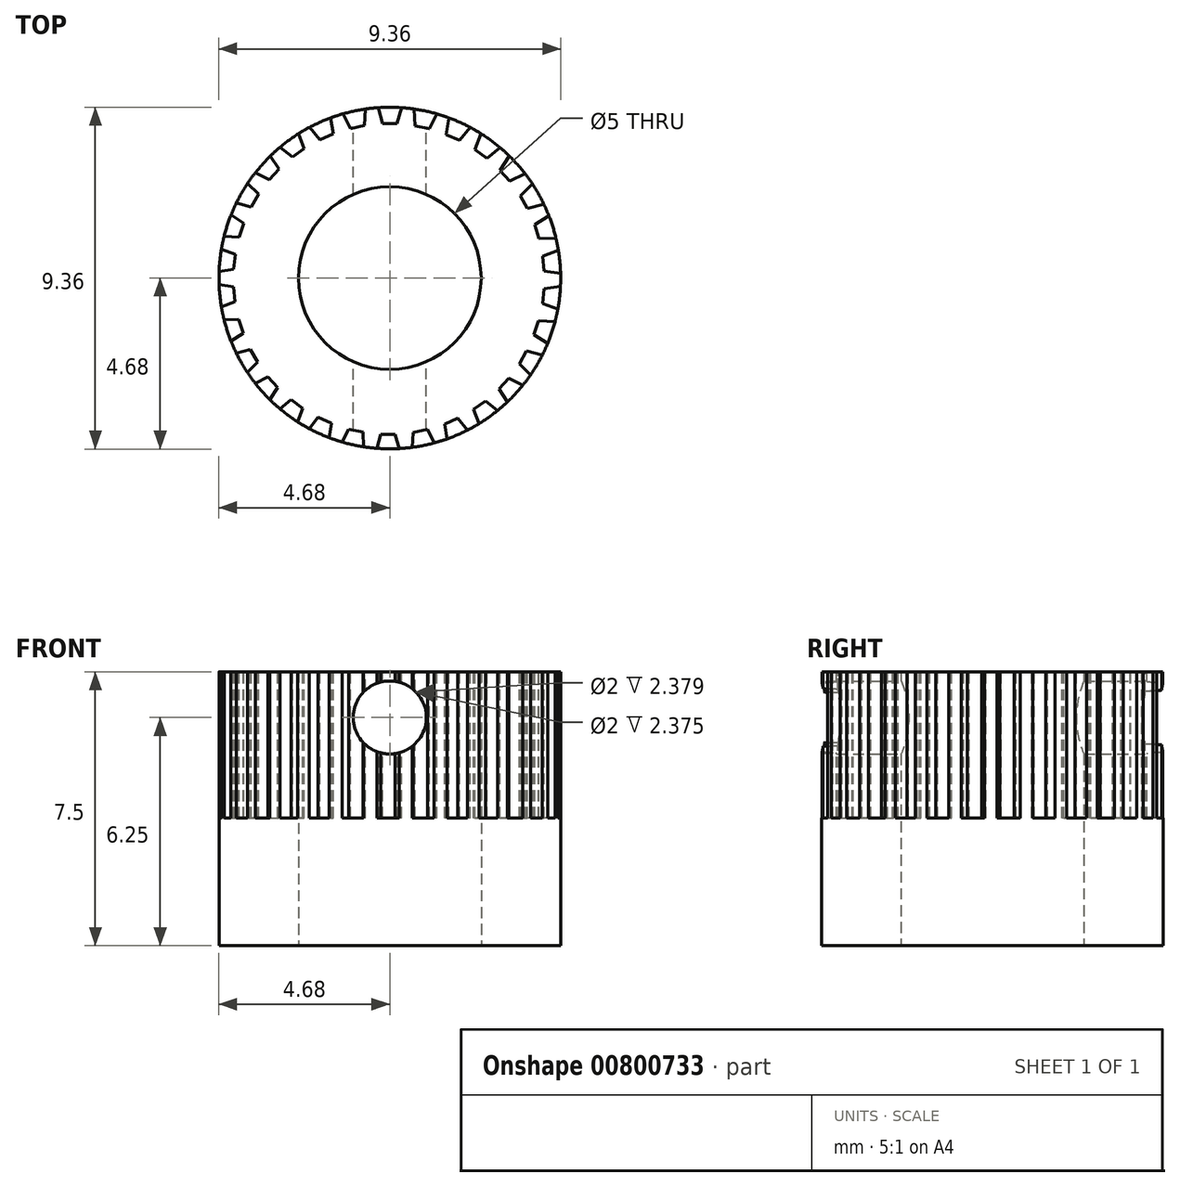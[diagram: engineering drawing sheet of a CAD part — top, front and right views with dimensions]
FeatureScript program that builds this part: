
annotation { "Feature Type Name" : "Feature", "Feature Type Description" : "" }
export const myFeature = defineFeature(function(context is Context, id is Id, definition is map)
    precondition{}
    {
        {
            var Q0;
            Q0=qCreatedBy(makeId("Top.planeOp"),FACE);
            var sketch = newSketch(context, id + "F0", { "sketchPlane" : qUnion([Q0])});
            skCircle(sketch, "E0", {"center": v(0, 0) * mm, "radius": 4.67 * mm});
            skCircle(sketch, "E1", {"center": v(0, 0) * mm, "radius": 2.5 * mm});
            skSolve(sketch);
        }
        {
            var Q0;
            Q0 = qSketchRegion(id + "F0", true);
            extrude(context, id + "F1", {"entities" : qUnion([Q0]), "depth" : 7.5 * mm, "offsetDistance" : 25 * mm});
        }
        {
            var Q0;
            Q0=makeQuery(id+"F1.opExtrude","CAP_FACE",FACE,{"disambiguationData":[OSD([sQuery(id+"F0.wireOp",EDGE,"E0"),sQuery(id+"F0.wireOp",EDGE,"E1")])],"isStart":false});
            var sketch = newSketch(context, id + "F2", { "sketchPlane" : qUnion([Q0])});
            skLineSegment(sketch, "E2", {"start": v(0, 5.22) * mm, "end": v(-0.47, 5.22) * mm});
            skLineSegment(sketch, "E3", {"start": v(-0.47, 5.22) * mm, "end": v(-0.2, 4.22) * mm});
            skLineSegment(sketch, "E4", {"start": v(-0.2, 4.22) * mm, "end": v(0, 4.22) * mm});
            skLineSegment(sketch, "E5", {"start": v(0, 4.22) * mm, "end": v(0, 5.22) * mm});
            skLineSegment(sketch, "E6.MirrorCS", {"start": v(0.2, 4.22) * mm, "end": v(0, 4.22) * mm});
            skLineSegment(sketch, "E7.MirrorCS", {"start": v(0, 5.22) * mm, "end": v(0.47, 5.22) * mm});
            skLineSegment(sketch, "E8.MirrorCS", {"start": v(0.47, 5.22) * mm, "end": v(0.2, 4.22) * mm});
            skLineSegment(sketch, "E9.1.0", {"start": v(-1.55, 5.02) * mm, "end": v(-1.08, 4.1) * mm});
            skLineSegment(sketch, "E9.1.1", {"start": v(-0.63, 5.21) * mm, "end": v(-0.69, 4.18) * mm});
            skLineSegment(sketch, "E9.1.2", {"start": v(-1.1, 5.12) * mm, "end": v(-0.63, 5.21) * mm});
            skLineSegment(sketch, "E9.1.3", {"start": v(-1.1, 5.12) * mm, "end": v(-1.55, 5.02) * mm});
            skLineSegment(sketch, "E9.1.4", {"start": v(-1.08, 4.1) * mm, "end": v(-0.88, 4.14) * mm});
            skLineSegment(sketch, "E9.1.5", {"start": v(-0.69, 4.18) * mm, "end": v(-0.88, 4.14) * mm});
            skLineSegment(sketch, "E9.2.0", {"start": v(-2.57, 4.6) * mm, "end": v(-1.91, 3.79) * mm});
            skLineSegment(sketch, "E9.2.1", {"start": v(-1.71, 4.97) * mm, "end": v(-1.55, 3.95) * mm});
            skLineSegment(sketch, "E9.2.2", {"start": v(-2.14, 4.78) * mm, "end": v(-1.71, 4.97) * mm});
            skLineSegment(sketch, "E9.2.3", {"start": v(-2.14, 4.78) * mm, "end": v(-2.57, 4.6) * mm});
            skLineSegment(sketch, "E9.2.4", {"start": v(-1.91, 3.79) * mm, "end": v(-1.73, 3.87) * mm});
            skLineSegment(sketch, "E9.2.5", {"start": v(-1.55, 3.95) * mm, "end": v(-1.73, 3.87) * mm});
            skLineSegment(sketch, "E9.3.0", {"start": v(-3.47, 3.96) * mm, "end": v(-2.66, 3.31) * mm});
            skLineSegment(sketch, "E9.3.1", {"start": v(-2.71, 4.51) * mm, "end": v(-2.34, 3.55) * mm});
            skLineSegment(sketch, "E9.3.2", {"start": v(-3.1, 4.24) * mm, "end": v(-2.71, 4.51) * mm});
            skLineSegment(sketch, "E9.3.3", {"start": v(-3.1, 4.24) * mm, "end": v(-3.47, 3.96) * mm});
            skLineSegment(sketch, "E9.3.4", {"start": v(-2.66, 3.31) * mm, "end": v(-2.5, 3.43) * mm});
            skLineSegment(sketch, "E9.3.5", {"start": v(-2.34, 3.55) * mm, "end": v(-2.5, 3.43) * mm});
            skLineSegment(sketch, "E9.4.0", {"start": v(-4.22, 3.16) * mm, "end": v(-3.3, 2.69) * mm});
            skLineSegment(sketch, "E9.4.1", {"start": v(-3.6, 3.85) * mm, "end": v(-3.03, 2.99) * mm});
            skLineSegment(sketch, "E9.4.2", {"start": v(-3.9, 3.5) * mm, "end": v(-3.6, 3.85) * mm});
            skLineSegment(sketch, "E9.4.3", {"start": v(-3.9, 3.5) * mm, "end": v(-4.22, 3.16) * mm});
            skLineSegment(sketch, "E9.4.4", {"start": v(-3.3, 2.69) * mm, "end": v(-3.17, 2.84) * mm});
            skLineSegment(sketch, "E9.4.5", {"start": v(-3.03, 2.99) * mm, "end": v(-3.17, 2.84) * mm});
            skLineSegment(sketch, "E9.5.0", {"start": v(-4.8, 2.22) * mm, "end": v(-3.8, 1.95) * mm});
            skLineSegment(sketch, "E9.5.1", {"start": v(-4.33, 3.03) * mm, "end": v(-3.6, 2.3) * mm});
            skLineSegment(sketch, "E9.5.2", {"start": v(-4.56, 2.62) * mm, "end": v(-4.33, 3.03) * mm});
            skLineSegment(sketch, "E9.5.3", {"start": v(-4.56, 2.62) * mm, "end": v(-4.8, 2.22) * mm});
            skLineSegment(sketch, "E9.5.4", {"start": v(-3.8, 1.95) * mm, "end": v(-3.7, 2.12) * mm});
            skLineSegment(sketch, "E9.5.5", {"start": v(-3.6, 2.3) * mm, "end": v(-3.7, 2.12) * mm});
            skLineSegment(sketch, "E9.6.0", {"start": v(-5.15, 1.18) * mm, "end": v(-4.12, 1.12) * mm});
            skLineSegment(sketch, "E9.6.1", {"start": v(-4.87, 2.07) * mm, "end": v(-4, 1.5) * mm});
            skLineSegment(sketch, "E9.6.2", {"start": v(-5.01, 1.62) * mm, "end": v(-4.87, 2.07) * mm});
            skLineSegment(sketch, "E9.6.3", {"start": v(-5.01, 1.62) * mm, "end": v(-5.15, 1.18) * mm});
            skLineSegment(sketch, "E9.6.4", {"start": v(-4.12, 1.12) * mm, "end": v(-4.06, 1.31) * mm});
            skLineSegment(sketch, "E9.6.5", {"start": v(-4, 1.5) * mm, "end": v(-4.06, 1.31) * mm});
            skLineSegment(sketch, "E9.7.0", {"start": v(-5.3, 0.08) * mm, "end": v(-4.27, 0.25) * mm});
            skLineSegment(sketch, "E9.7.1", {"start": v(-5.2, 1.01) * mm, "end": v(-4.23, 0.64) * mm});
            skLineSegment(sketch, "E9.7.2", {"start": v(-5.24, 0.55) * mm, "end": v(-5.2, 1.01) * mm});
            skLineSegment(sketch, "E9.7.3", {"start": v(-5.24, 0.55) * mm, "end": v(-5.3, 0.08) * mm});
            skLineSegment(sketch, "E9.7.4", {"start": v(-4.27, 0.25) * mm, "end": v(-4.25, 0.44) * mm});
            skLineSegment(sketch, "E9.7.5", {"start": v(-4.23, 0.64) * mm, "end": v(-4.25, 0.44) * mm});
            skLineSegment(sketch, "E9.8.0", {"start": v(-5.2, -1.01) * mm, "end": v(-4.23, -0.64) * mm});
            skLineSegment(sketch, "E9.8.1", {"start": v(-5.3, -0.08) * mm, "end": v(-4.28, -0.25) * mm});
            skLineSegment(sketch, "E9.8.2", {"start": v(-5.25, -0.55) * mm, "end": v(-5.3, -0.08) * mm});
            skLineSegment(sketch, "E9.8.3", {"start": v(-5.25, -0.55) * mm, "end": v(-5.2, -1.01) * mm});
            skLineSegment(sketch, "E9.8.4", {"start": v(-4.23, -0.64) * mm, "end": v(-4.25, -0.44) * mm});
            skLineSegment(sketch, "E9.8.5", {"start": v(-4.28, -0.25) * mm, "end": v(-4.25, -0.44) * mm});
            skLineSegment(sketch, "E9.9.0", {"start": v(-4.88, -2.07) * mm, "end": v(-4.01, -1.5) * mm});
            skLineSegment(sketch, "E9.9.1", {"start": v(-5.17, -1.18) * mm, "end": v(-4.14, -1.12) * mm});
            skLineSegment(sketch, "E9.9.2", {"start": v(-5.03, -1.62) * mm, "end": v(-5.17, -1.18) * mm});
            skLineSegment(sketch, "E9.9.3", {"start": v(-5.03, -1.62) * mm, "end": v(-4.88, -2.07) * mm});
            skLineSegment(sketch, "E9.9.4", {"start": v(-4.01, -1.5) * mm, "end": v(-4.07, -1.31) * mm});
            skLineSegment(sketch, "E9.9.5", {"start": v(-4.14, -1.12) * mm, "end": v(-4.07, -1.31) * mm});
            skLineSegment(sketch, "E9.10.0", {"start": v(-4.35, -3.03) * mm, "end": v(-3.62, -2.3) * mm});
            skLineSegment(sketch, "E9.10.1", {"start": v(-4.82, -2.22) * mm, "end": v(-3.82, -1.96) * mm});
            skLineSegment(sketch, "E9.10.2", {"start": v(-4.58, -2.63) * mm, "end": v(-4.82, -2.22) * mm});
            skLineSegment(sketch, "E9.10.3", {"start": v(-4.58, -2.63) * mm, "end": v(-4.35, -3.03) * mm});
            skLineSegment(sketch, "E9.10.4", {"start": v(-3.62, -2.3) * mm, "end": v(-3.72, -2.13) * mm});
            skLineSegment(sketch, "E9.10.5", {"start": v(-3.82, -1.96) * mm, "end": v(-3.72, -2.13) * mm});
            skLineSegment(sketch, "E9.11.0", {"start": v(-3.63, -3.87) * mm, "end": v(-3.07, -3) * mm});
            skLineSegment(sketch, "E9.11.1", {"start": v(-4.26, -3.17) * mm, "end": v(-3.33, -2.7) * mm});
            skLineSegment(sketch, "E9.11.2", {"start": v(-3.94, -3.52) * mm, "end": v(-4.26, -3.17) * mm});
            skLineSegment(sketch, "E9.11.3", {"start": v(-3.94, -3.52) * mm, "end": v(-3.63, -3.87) * mm});
            skLineSegment(sketch, "E9.11.4", {"start": v(-3.07, -3) * mm, "end": v(-3.2, -2.85) * mm});
            skLineSegment(sketch, "E9.11.5", {"start": v(-3.33, -2.7) * mm, "end": v(-3.2, -2.85) * mm});
            skLineSegment(sketch, "E9.12.0", {"start": v(-2.75, -4.53) * mm, "end": v(-2.38, -3.57) * mm});
            skLineSegment(sketch, "E9.12.1", {"start": v(-3.5, -3.98) * mm, "end": v(-2.7, -3.33) * mm});
            skLineSegment(sketch, "E9.12.2", {"start": v(-3.13, -4.26) * mm, "end": v(-3.5, -3.98) * mm});
            skLineSegment(sketch, "E9.12.3", {"start": v(-3.13, -4.26) * mm, "end": v(-2.75, -4.53) * mm});
            skLineSegment(sketch, "E9.12.4", {"start": v(-2.38, -3.57) * mm, "end": v(-2.54, -3.45) * mm});
            skLineSegment(sketch, "E9.12.5", {"start": v(-2.7, -3.33) * mm, "end": v(-2.54, -3.45) * mm});
            skLineSegment(sketch, "E9.13.0", {"start": v(-1.76, -5) * mm, "end": v(-1.6, -3.98) * mm});
            skLineSegment(sketch, "E9.13.1", {"start": v(-2.61, -4.62) * mm, "end": v(-1.96, -3.82) * mm});
            skLineSegment(sketch, "E9.13.2", {"start": v(-2.18, -4.81) * mm, "end": v(-2.61, -4.62) * mm});
            skLineSegment(sketch, "E9.13.3", {"start": v(-2.18, -4.81) * mm, "end": v(-1.76, -5) * mm});
            skLineSegment(sketch, "E9.13.4", {"start": v(-1.6, -3.98) * mm, "end": v(-1.78, -3.9) * mm});
            skLineSegment(sketch, "E9.13.5", {"start": v(-1.96, -3.82) * mm, "end": v(-1.78, -3.9) * mm});
            skLineSegment(sketch, "E9.14.0", {"start": v(-0.68, -5.25) * mm, "end": v(-0.74, -4.22) * mm});
            skLineSegment(sketch, "E9.14.1", {"start": v(-1.6, -5.06) * mm, "end": v(-1.13, -4.14) * mm});
            skLineSegment(sketch, "E9.14.2", {"start": v(-1.14, -5.16) * mm, "end": v(-1.6, -5.06) * mm});
            skLineSegment(sketch, "E9.14.3", {"start": v(-1.14, -5.16) * mm, "end": v(-0.68, -5.25) * mm});
            skLineSegment(sketch, "E9.14.4", {"start": v(-0.74, -4.22) * mm, "end": v(-0.93, -4.18) * mm});
            skLineSegment(sketch, "E9.14.5", {"start": v(-1.13, -4.14) * mm, "end": v(-0.93, -4.18) * mm});
            skLineSegment(sketch, "E9.15.0", {"start": v(0.42, -5.27) * mm, "end": v(0.15, -4.27) * mm});
            skLineSegment(sketch, "E9.15.1", {"start": v(-0.52, -5.27) * mm, "end": v(-0.25, -4.27) * mm});
            skLineSegment(sketch, "E9.15.2", {"start": v(-0.05, -5.28) * mm, "end": v(-0.52, -5.28) * mm});
            skLineSegment(sketch, "E9.15.3", {"start": v(-0.05, -5.27) * mm, "end": v(0.42, -5.27) * mm});
            skLineSegment(sketch, "E9.15.4", {"start": v(0.15, -4.28) * mm, "end": v(-0.05, -4.28) * mm});
            skLineSegment(sketch, "E9.15.5", {"start": v(-0.25, -4.28) * mm, "end": v(-0.05, -4.28) * mm});
            skLineSegment(sketch, "E9.16.0", {"start": v(1.5, -5.07) * mm, "end": v(1.03, -4.15) * mm});
            skLineSegment(sketch, "E9.16.1", {"start": v(0.58, -5.26) * mm, "end": v(0.64, -4.23) * mm});
            skLineSegment(sketch, "E9.16.2", {"start": v(1.04, -5.17) * mm, "end": v(0.58, -5.26) * mm});
            skLineSegment(sketch, "E9.16.3", {"start": v(1.04, -5.17) * mm, "end": v(1.5, -5.07) * mm});
            skLineSegment(sketch, "E9.16.4", {"start": v(1.03, -4.15) * mm, "end": v(0.83, -4.19) * mm});
            skLineSegment(sketch, "E9.16.5", {"start": v(0.64, -4.23) * mm, "end": v(0.83, -4.19) * mm});
            skLineSegment(sketch, "E9.17.0", {"start": v(2.52, -4.64) * mm, "end": v(1.86, -3.84) * mm});
            skLineSegment(sketch, "E9.17.1", {"start": v(1.66, -5.02) * mm, "end": v(1.5, -4) * mm});
            skLineSegment(sketch, "E9.17.2", {"start": v(2.09, -4.83) * mm, "end": v(1.66, -5.02) * mm});
            skLineSegment(sketch, "E9.17.3", {"start": v(2.09, -4.83) * mm, "end": v(2.52, -4.64) * mm});
            skLineSegment(sketch, "E9.17.4", {"start": v(1.86, -3.84) * mm, "end": v(1.68, -3.92) * mm});
            skLineSegment(sketch, "E9.17.5", {"start": v(1.5, -4) * mm, "end": v(1.68, -3.92) * mm});
            skLineSegment(sketch, "E9.18.0", {"start": v(3.42, -4.01) * mm, "end": v(2.61, -3.36) * mm});
            skLineSegment(sketch, "E9.18.1", {"start": v(2.66, -4.56) * mm, "end": v(2.3, -3.6) * mm});
            skLineSegment(sketch, "E9.18.2", {"start": v(3.04, -4.29) * mm, "end": v(2.66, -4.56) * mm});
            skLineSegment(sketch, "E9.18.3", {"start": v(3.04, -4.29) * mm, "end": v(3.42, -4.01) * mm});
            skLineSegment(sketch, "E9.18.4", {"start": v(2.61, -3.36) * mm, "end": v(2.45, -3.48) * mm});
            skLineSegment(sketch, "E9.18.5", {"start": v(2.3, -3.6) * mm, "end": v(2.45, -3.48) * mm});
            skLineSegment(sketch, "E9.19.0", {"start": v(4.17, -3.2) * mm, "end": v(3.25, -2.74) * mm});
            skLineSegment(sketch, "E9.19.1", {"start": v(3.55, -3.9) * mm, "end": v(2.98, -3.04) * mm});
            skLineSegment(sketch, "E9.19.2", {"start": v(3.86, -3.56) * mm, "end": v(3.55, -3.9) * mm});
            skLineSegment(sketch, "E9.19.3", {"start": v(3.86, -3.56) * mm, "end": v(4.17, -3.2) * mm});
            skLineSegment(sketch, "E9.19.4", {"start": v(3.25, -2.74) * mm, "end": v(3.12, -2.89) * mm});
            skLineSegment(sketch, "E9.19.5", {"start": v(2.98, -3.04) * mm, "end": v(3.12, -2.89) * mm});
            skLineSegment(sketch, "E9.20.0", {"start": v(4.74, -2.27) * mm, "end": v(3.74, -2) * mm});
            skLineSegment(sketch, "E9.20.1", {"start": v(4.28, -3.08) * mm, "end": v(3.54, -2.34) * mm});
            skLineSegment(sketch, "E9.20.2", {"start": v(4.5, -2.67) * mm, "end": v(4.28, -3.08) * mm});
            skLineSegment(sketch, "E9.20.3", {"start": v(4.5, -2.67) * mm, "end": v(4.74, -2.27) * mm});
            skLineSegment(sketch, "E9.20.4", {"start": v(3.74, -2) * mm, "end": v(3.64, -2.17) * mm});
            skLineSegment(sketch, "E9.20.5", {"start": v(3.54, -2.34) * mm, "end": v(3.64, -2.17) * mm});
            skLineSegment(sketch, "E9.21.0", {"start": v(5.1, -1.23) * mm, "end": v(4.07, -1.17) * mm});
            skLineSegment(sketch, "E9.21.1", {"start": v(4.82, -2.12) * mm, "end": v(3.95, -1.55) * mm});
            skLineSegment(sketch, "E9.21.2", {"start": v(4.96, -1.67) * mm, "end": v(4.82, -2.12) * mm});
            skLineSegment(sketch, "E9.21.3", {"start": v(4.96, -1.67) * mm, "end": v(5.1, -1.23) * mm});
            skLineSegment(sketch, "E9.21.4", {"start": v(4.07, -1.17) * mm, "end": v(4, -1.36) * mm});
            skLineSegment(sketch, "E9.21.5", {"start": v(3.95, -1.55) * mm, "end": v(4, -1.36) * mm});
            skLineSegment(sketch, "E9.22.0", {"start": v(5.24, -0.13) * mm, "end": v(4.22, -0.3) * mm});
            skLineSegment(sketch, "E9.22.1", {"start": v(5.14, -1.06) * mm, "end": v(4.18, -0.7) * mm});
            skLineSegment(sketch, "E9.22.2", {"start": v(5.2, -0.6) * mm, "end": v(5.14, -1.06) * mm});
            skLineSegment(sketch, "E9.22.3", {"start": v(5.2, -0.6) * mm, "end": v(5.24, -0.13) * mm});
            skLineSegment(sketch, "E9.22.4", {"start": v(4.22, -0.3) * mm, "end": v(4.2, -0.5) * mm});
            skLineSegment(sketch, "E9.22.5", {"start": v(4.18, -0.7) * mm, "end": v(4.2, -0.5) * mm});
            skLineSegment(sketch, "E9.23.0", {"start": v(5.15, 0.96) * mm, "end": v(4.18, 0.6) * mm});
            skLineSegment(sketch, "E9.23.1", {"start": v(5.25, 0.03) * mm, "end": v(4.23, 0.2) * mm});
            skLineSegment(sketch, "E9.23.2", {"start": v(5.2, 0.5) * mm, "end": v(5.25, 0.03) * mm});
            skLineSegment(sketch, "E9.23.3", {"start": v(5.2, 0.5) * mm, "end": v(5.15, 0.96) * mm});
            skLineSegment(sketch, "E9.23.4", {"start": v(4.18, 0.6) * mm, "end": v(4.2, 0.4) * mm});
            skLineSegment(sketch, "E9.23.5", {"start": v(4.23, 0.2) * mm, "end": v(4.2, 0.4) * mm});
            skLineSegment(sketch, "E9.24.0", {"start": v(4.83, 2.02) * mm, "end": v(3.96, 1.45) * mm});
            skLineSegment(sketch, "E9.24.1", {"start": v(5.12, 1.13) * mm, "end": v(4.09, 1.07) * mm});
            skLineSegment(sketch, "E9.24.2", {"start": v(4.98, 1.57) * mm, "end": v(5.12, 1.13) * mm});
            skLineSegment(sketch, "E9.24.3", {"start": v(4.98, 1.57) * mm, "end": v(4.83, 2.02) * mm});
            skLineSegment(sketch, "E9.24.4", {"start": v(3.96, 1.45) * mm, "end": v(4.02, 1.26) * mm});
            skLineSegment(sketch, "E9.24.5", {"start": v(4.09, 1.07) * mm, "end": v(4.02, 1.26) * mm});
            skLineSegment(sketch, "E9.25.0", {"start": v(4.3, 2.98) * mm, "end": v(3.57, 2.25) * mm});
            skLineSegment(sketch, "E9.25.1", {"start": v(4.77, 2.17) * mm, "end": v(3.77, 1.9) * mm});
            skLineSegment(sketch, "E9.25.2", {"start": v(4.53, 2.58) * mm, "end": v(4.77, 2.17) * mm});
            skLineSegment(sketch, "E9.25.3", {"start": v(4.53, 2.58) * mm, "end": v(4.3, 2.98) * mm});
            skLineSegment(sketch, "E9.25.4", {"start": v(3.57, 2.25) * mm, "end": v(3.67, 2.08) * mm});
            skLineSegment(sketch, "E9.25.5", {"start": v(3.77, 1.9) * mm, "end": v(3.67, 2.08) * mm});
            skLineSegment(sketch, "E9.26.0", {"start": v(3.58, 3.82) * mm, "end": v(3.02, 2.95) * mm});
            skLineSegment(sketch, "E9.26.1", {"start": v(4.2, 3.12) * mm, "end": v(3.28, 2.65) * mm});
            skLineSegment(sketch, "E9.26.2", {"start": v(3.9, 3.47) * mm, "end": v(4.2, 3.12) * mm});
            skLineSegment(sketch, "E9.26.3", {"start": v(3.9, 3.47) * mm, "end": v(3.58, 3.82) * mm});
            skLineSegment(sketch, "E9.26.4", {"start": v(3.02, 2.95) * mm, "end": v(3.15, 2.8) * mm});
            skLineSegment(sketch, "E9.26.5", {"start": v(3.28, 2.65) * mm, "end": v(3.15, 2.8) * mm});
            skLineSegment(sketch, "E9.27.0", {"start": v(2.7, 4.48) * mm, "end": v(2.33, 3.52) * mm});
            skLineSegment(sketch, "E9.27.1", {"start": v(3.46, 3.93) * mm, "end": v(2.66, 3.28) * mm});
            skLineSegment(sketch, "E9.27.2", {"start": v(3.08, 4.2) * mm, "end": v(3.46, 3.93) * mm});
            skLineSegment(sketch, "E9.27.3", {"start": v(3.08, 4.2) * mm, "end": v(2.7, 4.48) * mm});
            skLineSegment(sketch, "E9.27.4", {"start": v(2.33, 3.52) * mm, "end": v(2.5, 3.4) * mm});
            skLineSegment(sketch, "E9.27.5", {"start": v(2.66, 3.28) * mm, "end": v(2.5, 3.4) * mm});
            skLineSegment(sketch, "E9.28.0", {"start": v(1.7, 4.95) * mm, "end": v(1.54, 3.93) * mm});
            skLineSegment(sketch, "E9.28.1", {"start": v(2.56, 4.57) * mm, "end": v(1.9, 3.77) * mm});
            skLineSegment(sketch, "E9.28.2", {"start": v(2.13, 4.76) * mm, "end": v(2.56, 4.57) * mm});
            skLineSegment(sketch, "E9.28.3", {"start": v(2.13, 4.76) * mm, "end": v(1.7, 4.95) * mm});
            skLineSegment(sketch, "E9.28.4", {"start": v(1.54, 3.93) * mm, "end": v(1.73, 3.85) * mm});
            skLineSegment(sketch, "E9.28.5", {"start": v(1.9, 3.77) * mm, "end": v(1.73, 3.85) * mm});
            skLineSegment(sketch, "E9.29.0", {"start": v(0.63, 5.2) * mm, "end": v(0.69, 4.17) * mm});
            skLineSegment(sketch, "E9.29.1", {"start": v(1.55, 5) * mm, "end": v(1.08, 4.09) * mm});
            skLineSegment(sketch, "E9.29.2", {"start": v(1.1, 5.1) * mm, "end": v(1.55, 5) * mm});
            skLineSegment(sketch, "E9.29.3", {"start": v(1.1, 5.1) * mm, "end": v(0.63, 5.2) * mm});
            skLineSegment(sketch, "E9.29.4", {"start": v(0.69, 4.17) * mm, "end": v(0.88, 4.13) * mm});
            skLineSegment(sketch, "E9.29.5", {"start": v(1.08, 4.09) * mm, "end": v(0.88, 4.13) * mm});
            skPoint(sketch, "E9.center", {"position": v(-0.02, -0.02) * mm});
            skSolve(sketch);
        }
        {
            var Q0;
            {var subQ1=sQuery(id+"F2.wireOp",EDGE,"E9.12.4");Q0=makeQuery(id+"F2.imprint","IMPRINT",FACE,{"disambiguationData":[TD([[makeQuery(id+"F2.imprint","IMPRINT",EDGE,{"derivedFrom":subQ1}),1.0]])]});}
            var Q1;
            {var subQ6=sQuery(id+"F2.wireOp",EDGE,"E9.13.4");Q1=makeQuery(id+"F2.imprint","IMPRINT",FACE,{"disambiguationData":[TD([[makeQuery(id+"F2.imprint","IMPRINT",EDGE,{"derivedFrom":subQ6}),1.0]])]});}
            var Q2;
            {var subQ1=sQuery(id+"F2.wireOp",EDGE,"E9.14.4");Q2=makeQuery(id+"F2.imprint","IMPRINT",FACE,{"disambiguationData":[TD([[makeQuery(id+"F2.imprint","IMPRINT",EDGE,{"derivedFrom":subQ1}),1.0]])]});}
            var Q3;
            {var subQ1=sQuery(id+"F2.wireOp",EDGE,"E9.15.4");Q3=makeQuery(id+"F2.imprint","IMPRINT",FACE,{"disambiguationData":[TD([[makeQuery(id+"F2.imprint","IMPRINT",EDGE,{"derivedFrom":subQ1}),1.0]])]});}
            var Q4;
            {var subQ1=sQuery(id+"F2.wireOp",EDGE,"E9.11.4");Q4=makeQuery(id+"F2.imprint","IMPRINT",FACE,{"disambiguationData":[TD([[makeQuery(id+"F2.imprint","IMPRINT",EDGE,{"derivedFrom":subQ1}),1.0]])]});}
            var Q5;
            {var subQ1=sQuery(id+"F2.wireOp",EDGE,"E9.10.4");Q5=makeQuery(id+"F2.imprint","IMPRINT",FACE,{"disambiguationData":[TD([[makeQuery(id+"F2.imprint","IMPRINT",EDGE,{"derivedFrom":subQ1}),1.0]])]});}
            var Q6;
            {var subQ1=sQuery(id+"F2.wireOp",EDGE,"E9.9.4");Q6=makeQuery(id+"F2.imprint","IMPRINT",FACE,{"disambiguationData":[TD([[makeQuery(id+"F2.imprint","IMPRINT",EDGE,{"derivedFrom":subQ1}),1.0]])]});}
            var Q7;
            {var subQ1=sQuery(id+"F2.wireOp",EDGE,"E9.8.4");Q7=makeQuery(id+"F2.imprint","IMPRINT",FACE,{"disambiguationData":[TD([[makeQuery(id+"F2.imprint","IMPRINT",EDGE,{"derivedFrom":subQ1}),1.0]])]});}
            var Q8;
            {var subQ1=sQuery(id+"F2.wireOp",EDGE,"E9.7.4");Q8=makeQuery(id+"F2.imprint","IMPRINT",FACE,{"disambiguationData":[TD([[makeQuery(id+"F2.imprint","IMPRINT",EDGE,{"derivedFrom":subQ1}),1.0]])]});}
            var Q9;
            {var subQ1=sQuery(id+"F2.wireOp",EDGE,"E9.6.4");Q9=makeQuery(id+"F2.imprint","IMPRINT",FACE,{"disambiguationData":[TD([[makeQuery(id+"F2.imprint","IMPRINT",EDGE,{"derivedFrom":subQ1}),1.0]])]});}
            var Q10;
            {var subQ1=sQuery(id+"F2.wireOp",EDGE,"E9.5.4");Q10=makeQuery(id+"F2.imprint","IMPRINT",FACE,{"disambiguationData":[TD([[makeQuery(id+"F2.imprint","IMPRINT",EDGE,{"derivedFrom":subQ1}),1.0]])]});}
            var Q11;
            {var subQ1=sQuery(id+"F2.wireOp",EDGE,"E9.4.4");Q11=makeQuery(id+"F2.imprint","IMPRINT",FACE,{"disambiguationData":[TD([[makeQuery(id+"F2.imprint","IMPRINT",EDGE,{"derivedFrom":subQ1}),1.0]])]});}
            var Q12;
            {var subQ1=sQuery(id+"F2.wireOp",EDGE,"E9.3.4");Q12=makeQuery(id+"F2.imprint","IMPRINT",FACE,{"disambiguationData":[TD([[makeQuery(id+"F2.imprint","IMPRINT",EDGE,{"derivedFrom":subQ1}),1.0]])]});}
            var Q13;
            {var subQ6=sQuery(id+"F2.wireOp",EDGE,"E9.2.4");Q13=makeQuery(id+"F2.imprint","IMPRINT",FACE,{"disambiguationData":[TD([[makeQuery(id+"F2.imprint","IMPRINT",EDGE,{"derivedFrom":subQ6}),1.0]])]});}
            var Q14;
            {var subQ1=sQuery(id+"F2.wireOp",EDGE,"E9.1.4");Q14=makeQuery(id+"F2.imprint","IMPRINT",FACE,{"disambiguationData":[TD([[makeQuery(id+"F2.imprint","IMPRINT",EDGE,{"derivedFrom":subQ1}),1.0]])]});}
            var Q15;
            {var subQ0=sQuery(id+"F2.wireOp",EDGE,"E4");Q15=makeQuery(id+"F2.imprint","IMPRINT",FACE,{"disambiguationData":[TD([[makeQuery(id+"F2.imprint","IMPRINT",EDGE,{"derivedFrom":subQ0}),1.0]])]});}
            var Q16;
            {var subQ0=sQuery(id+"F2.wireOp",EDGE,"E6.MirrorCS");Q16=makeQuery(id+"F2.imprint","IMPRINT",FACE,{"disambiguationData":[TD([[makeQuery(id+"F2.imprint","IMPRINT",EDGE,{"derivedFrom":subQ0}),-1.0]])]});}
            var Q17;
            {var subQ1=sQuery(id+"F2.wireOp",EDGE,"E9.51.4");Q17=makeQuery(id+"F2.imprint","IMPRINT",FACE,{"disambiguationData":[TD([[makeQuery(id+"F2.imprint","IMPRINT",EDGE,{"derivedFrom":subQ1}),1.0]])]});}
            var Q18;
            {var subQ1=sQuery(id+"F2.wireOp",EDGE,"E9.50.4");Q18=makeQuery(id+"F2.imprint","IMPRINT",FACE,{"disambiguationData":[TD([[makeQuery(id+"F2.imprint","IMPRINT",EDGE,{"derivedFrom":subQ1}),1.0]])]});}
            var Q19;
            {var subQ1=sQuery(id+"F2.wireOp",EDGE,"E9.49.4");Q19=makeQuery(id+"F2.imprint","IMPRINT",FACE,{"disambiguationData":[TD([[makeQuery(id+"F2.imprint","IMPRINT",EDGE,{"derivedFrom":subQ1}),1.0]])]});}
            var Q20;
            {var subQ1=sQuery(id+"F2.wireOp",EDGE,"E9.48.4");Q20=makeQuery(id+"F2.imprint","IMPRINT",FACE,{"disambiguationData":[TD([[makeQuery(id+"F2.imprint","IMPRINT",EDGE,{"derivedFrom":subQ1}),1.0]])]});}
            var Q21;
            {var subQ1=sQuery(id+"F2.wireOp",EDGE,"E9.47.4");Q21=makeQuery(id+"F2.imprint","IMPRINT",FACE,{"disambiguationData":[TD([[makeQuery(id+"F2.imprint","IMPRINT",EDGE,{"derivedFrom":subQ1}),1.0]])]});}
            var Q22;
            {var subQ6=sQuery(id+"F2.wireOp",EDGE,"E9.46.4");Q22=makeQuery(id+"F2.imprint","IMPRINT",FACE,{"disambiguationData":[TD([[makeQuery(id+"F2.imprint","IMPRINT",EDGE,{"derivedFrom":subQ6}),1.0]])]});}
            var Q23;
            {var subQ1=sQuery(id+"F2.wireOp",EDGE,"E9.45.4");Q23=makeQuery(id+"F2.imprint","IMPRINT",FACE,{"disambiguationData":[TD([[makeQuery(id+"F2.imprint","IMPRINT",EDGE,{"derivedFrom":subQ1}),1.0]])]});}
            var Q24;
            {var subQ1=sQuery(id+"F2.wireOp",EDGE,"E9.44.4");Q24=makeQuery(id+"F2.imprint","IMPRINT",FACE,{"disambiguationData":[TD([[makeQuery(id+"F2.imprint","IMPRINT",EDGE,{"derivedFrom":subQ1}),1.0]])]});}
            var Q25;
            {var subQ1=sQuery(id+"F2.wireOp",EDGE,"E9.43.4");Q25=makeQuery(id+"F2.imprint","IMPRINT",FACE,{"disambiguationData":[TD([[makeQuery(id+"F2.imprint","IMPRINT",EDGE,{"derivedFrom":subQ1}),1.0]])]});}
            var Q26;
            {var subQ1=sQuery(id+"F2.wireOp",EDGE,"E9.42.4");Q26=makeQuery(id+"F2.imprint","IMPRINT",FACE,{"disambiguationData":[TD([[makeQuery(id+"F2.imprint","IMPRINT",EDGE,{"derivedFrom":subQ1}),1.0]])]});}
            var Q27;
            {var subQ1=sQuery(id+"F2.wireOp",EDGE,"E9.41.4");Q27=makeQuery(id+"F2.imprint","IMPRINT",FACE,{"disambiguationData":[TD([[makeQuery(id+"F2.imprint","IMPRINT",EDGE,{"derivedFrom":subQ1}),1.0]])]});}
            var Q28;
            {var subQ1=sQuery(id+"F2.wireOp",EDGE,"E9.40.4");Q28=makeQuery(id+"F2.imprint","IMPRINT",FACE,{"disambiguationData":[TD([[makeQuery(id+"F2.imprint","IMPRINT",EDGE,{"derivedFrom":subQ1}),1.0]])]});}
            var Q29;
            {var subQ1=sQuery(id+"F2.wireOp",EDGE,"E9.39.4");Q29=makeQuery(id+"F2.imprint","IMPRINT",FACE,{"disambiguationData":[TD([[makeQuery(id+"F2.imprint","IMPRINT",EDGE,{"derivedFrom":subQ1}),1.0]])]});}
            var Q30;
            {var subQ1=sQuery(id+"F2.wireOp",EDGE,"E9.38.4");Q30=makeQuery(id+"F2.imprint","IMPRINT",FACE,{"disambiguationData":[TD([[makeQuery(id+"F2.imprint","IMPRINT",EDGE,{"derivedFrom":subQ1}),1.0]])]});}
            var Q31;
            {var subQ1=sQuery(id+"F2.wireOp",EDGE,"E9.37.4");Q31=makeQuery(id+"F2.imprint","IMPRINT",FACE,{"disambiguationData":[TD([[makeQuery(id+"F2.imprint","IMPRINT",EDGE,{"derivedFrom":subQ1}),1.0]])]});}
            var Q32;
            {var subQ1=sQuery(id+"F2.wireOp",EDGE,"E9.36.4");Q32=makeQuery(id+"F2.imprint","IMPRINT",FACE,{"disambiguationData":[TD([[makeQuery(id+"F2.imprint","IMPRINT",EDGE,{"derivedFrom":subQ1}),1.0]])]});}
            var Q33;
            {var subQ6=sQuery(id+"F2.wireOp",EDGE,"E9.35.4");Q33=makeQuery(id+"F2.imprint","IMPRINT",FACE,{"disambiguationData":[TD([[makeQuery(id+"F2.imprint","IMPRINT",EDGE,{"derivedFrom":subQ6}),1.0]])]});}
            var Q34;
            {var subQ1=sQuery(id+"F2.wireOp",EDGE,"E9.34.4");Q34=makeQuery(id+"F2.imprint","IMPRINT",FACE,{"disambiguationData":[TD([[makeQuery(id+"F2.imprint","IMPRINT",EDGE,{"derivedFrom":subQ1}),1.0]])]});}
            var Q35;
            {var subQ1=sQuery(id+"F2.wireOp",EDGE,"E9.33.4");Q35=makeQuery(id+"F2.imprint","IMPRINT",FACE,{"disambiguationData":[TD([[makeQuery(id+"F2.imprint","IMPRINT",EDGE,{"derivedFrom":subQ1}),1.0]])]});}
            var Q36;
            {var subQ1=sQuery(id+"F2.wireOp",EDGE,"E9.32.4");Q36=makeQuery(id+"F2.imprint","IMPRINT",FACE,{"disambiguationData":[TD([[makeQuery(id+"F2.imprint","IMPRINT",EDGE,{"derivedFrom":subQ1}),1.0]])]});}
            var Q37;
            {var subQ1=sQuery(id+"F2.wireOp",EDGE,"E9.31.4");Q37=makeQuery(id+"F2.imprint","IMPRINT",FACE,{"disambiguationData":[TD([[makeQuery(id+"F2.imprint","IMPRINT",EDGE,{"derivedFrom":subQ1}),1.0]])]});}
            var Q38;
            {var subQ1=sQuery(id+"F2.wireOp",EDGE,"E9.30.4");Q38=makeQuery(id+"F2.imprint","IMPRINT",FACE,{"disambiguationData":[TD([[makeQuery(id+"F2.imprint","IMPRINT",EDGE,{"derivedFrom":subQ1}),1.0]])]});}
            var Q39;
            {var subQ1=sQuery(id+"F2.wireOp",EDGE,"E9.29.4");Q39=makeQuery(id+"F2.imprint","IMPRINT",FACE,{"disambiguationData":[TD([[makeQuery(id+"F2.imprint","IMPRINT",EDGE,{"derivedFrom":subQ1}),1.0]])]});}
            var Q40;
            {var subQ1=sQuery(id+"F2.wireOp",EDGE,"E9.28.4");Q40=makeQuery(id+"F2.imprint","IMPRINT",FACE,{"disambiguationData":[TD([[makeQuery(id+"F2.imprint","IMPRINT",EDGE,{"derivedFrom":subQ1}),1.0]])]});}
            var Q41;
            {var subQ1=sQuery(id+"F2.wireOp",EDGE,"E9.27.4");Q41=makeQuery(id+"F2.imprint","IMPRINT",FACE,{"disambiguationData":[TD([[makeQuery(id+"F2.imprint","IMPRINT",EDGE,{"derivedFrom":subQ1}),1.0]])]});}
            var Q42;
            {var subQ1=sQuery(id+"F2.wireOp",EDGE,"E9.26.4");Q42=makeQuery(id+"F2.imprint","IMPRINT",FACE,{"disambiguationData":[TD([[makeQuery(id+"F2.imprint","IMPRINT",EDGE,{"derivedFrom":subQ1}),1.0]])]});}
            var Q43;
            {var subQ1=sQuery(id+"F2.wireOp",EDGE,"E9.25.4");Q43=makeQuery(id+"F2.imprint","IMPRINT",FACE,{"disambiguationData":[TD([[makeQuery(id+"F2.imprint","IMPRINT",EDGE,{"derivedFrom":subQ1}),1.0]])]});}
            var Q44;
            {var subQ6=sQuery(id+"F2.wireOp",EDGE,"E9.24.4");Q44=makeQuery(id+"F2.imprint","IMPRINT",FACE,{"disambiguationData":[TD([[makeQuery(id+"F2.imprint","IMPRINT",EDGE,{"derivedFrom":subQ6}),1.0]])]});}
            var Q45;
            {var subQ1=sQuery(id+"F2.wireOp",EDGE,"E9.23.4");Q45=makeQuery(id+"F2.imprint","IMPRINT",FACE,{"disambiguationData":[TD([[makeQuery(id+"F2.imprint","IMPRINT",EDGE,{"derivedFrom":subQ1}),1.0]])]});}
            var Q46;
            {var subQ1=sQuery(id+"F2.wireOp",EDGE,"E9.22.4");Q46=makeQuery(id+"F2.imprint","IMPRINT",FACE,{"disambiguationData":[TD([[makeQuery(id+"F2.imprint","IMPRINT",EDGE,{"derivedFrom":subQ1}),1.0]])]});}
            var Q47;
            {var subQ1=sQuery(id+"F2.wireOp",EDGE,"E9.21.4");Q47=makeQuery(id+"F2.imprint","IMPRINT",FACE,{"disambiguationData":[TD([[makeQuery(id+"F2.imprint","IMPRINT",EDGE,{"derivedFrom":subQ1}),1.0]])]});}
            var Q48;
            {var subQ1=sQuery(id+"F2.wireOp",EDGE,"E9.16.4");Q48=makeQuery(id+"F2.imprint","IMPRINT",FACE,{"disambiguationData":[TD([[makeQuery(id+"F2.imprint","IMPRINT",EDGE,{"derivedFrom":subQ1}),1.0]])]});}
            var Q49;
            {var subQ1=sQuery(id+"F2.wireOp",EDGE,"E9.17.4");Q49=makeQuery(id+"F2.imprint","IMPRINT",FACE,{"disambiguationData":[TD([[makeQuery(id+"F2.imprint","IMPRINT",EDGE,{"derivedFrom":subQ1}),1.0]])]});}
            var Q50;
            {var subQ1=sQuery(id+"F2.wireOp",EDGE,"E9.18.4");Q50=makeQuery(id+"F2.imprint","IMPRINT",FACE,{"disambiguationData":[TD([[makeQuery(id+"F2.imprint","IMPRINT",EDGE,{"derivedFrom":subQ1}),1.0]])]});}
            var Q51;
            {var subQ1=sQuery(id+"F2.wireOp",EDGE,"E9.19.4");Q51=makeQuery(id+"F2.imprint","IMPRINT",FACE,{"disambiguationData":[TD([[makeQuery(id+"F2.imprint","IMPRINT",EDGE,{"derivedFrom":subQ1}),1.0]])]});}
            var Q52;
            {var subQ1=sQuery(id+"F2.wireOp",EDGE,"E9.20.4");Q52=makeQuery(id+"F2.imprint","IMPRINT",FACE,{"disambiguationData":[TD([[makeQuery(id+"F2.imprint","IMPRINT",EDGE,{"derivedFrom":subQ1}),1.0]])]});}
            var Q53;
            {var subQ1=sQuery(id+"F2.wireOp",EDGE,"37aef037-0f85-4e1d-9003-c95457172074.12.59.0");Q53=makeQuery(id+"F2.imprint","IMPRINT",FACE,{"disambiguationData":[TD([[makeQuery(id+"F2.imprint","IMPRINT",EDGE,{"derivedFrom":subQ1}),1.0]])]});}
            var Q54;
            {var subQ1=sQuery(id+"F2.wireOp",EDGE,"37aef037-0f85-4e1d-9003-c95457172074.12.58.0");Q54=makeQuery(id+"F2.imprint","IMPRINT",FACE,{"disambiguationData":[TD([[makeQuery(id+"F2.imprint","IMPRINT",EDGE,{"derivedFrom":subQ1}),1.0]])]});}
            var Q55;
            {var subQ1=sQuery(id+"F2.wireOp",EDGE,"37aef037-0f85-4e1d-9003-c95457172074.12.57.0");Q55=makeQuery(id+"F2.imprint","IMPRINT",FACE,{"disambiguationData":[TD([[makeQuery(id+"F2.imprint","IMPRINT",EDGE,{"derivedFrom":subQ1}),1.0]])]});}
            var Q56;
            {var subQ1=sQuery(id+"F2.wireOp",EDGE,"37aef037-0f85-4e1d-9003-c95457172074.12.56.0");Q56=makeQuery(id+"F2.imprint","IMPRINT",FACE,{"disambiguationData":[TD([[makeQuery(id+"F2.imprint","IMPRINT",EDGE,{"derivedFrom":subQ1}),1.0]])]});}
            var Q57;
            {var subQ1=sQuery(id+"F2.wireOp",EDGE,"37aef037-0f85-4e1d-9003-c95457172074.12.55.0");Q57=makeQuery(id+"F2.imprint","IMPRINT",FACE,{"disambiguationData":[TD([[makeQuery(id+"F2.imprint","IMPRINT",EDGE,{"derivedFrom":subQ1}),1.0]])]});}
            var Q58;
            {var subQ1=sQuery(id+"F2.wireOp",EDGE,"37aef037-0f85-4e1d-9003-c95457172074.12.54.0");Q58=makeQuery(id+"F2.imprint","IMPRINT",FACE,{"disambiguationData":[TD([[makeQuery(id+"F2.imprint","IMPRINT",EDGE,{"derivedFrom":subQ1}),1.0]])]});}
            var Q59;
            {var subQ1=sQuery(id+"F2.wireOp",EDGE,"442e21be-9c72-443b-8df6-9a8ef3729ca6.12.53.0");Q59=makeQuery(id+"F2.imprint","IMPRINT",FACE,{"disambiguationData":[TD([[makeQuery(id+"F2.imprint","IMPRINT",EDGE,{"derivedFrom":subQ1}),1.0]])]});}
            var Q60;
            {var subQ6=sQuery(id+"F2.wireOp",EDGE,"442e21be-9c72-443b-8df6-9a8ef3729ca6.12.52.0");Q60=makeQuery(id+"F2.imprint","IMPRINT",FACE,{"disambiguationData":[TD([[makeQuery(id+"F2.imprint","IMPRINT",EDGE,{"derivedFrom":subQ6}),1.0]])]});}
            var Q61;
            {var subQ1=sQuery(id+"F2.wireOp",EDGE,"5d3470c4-9be6-4ab4-af18-11b8a38611c9.12.35.0");Q61=makeQuery(id+"F2.imprint","IMPRINT",FACE,{"disambiguationData":[TD([[makeQuery(id+"F2.imprint","IMPRINT",EDGE,{"derivedFrom":subQ1}),1.0]])]});}
            var Q62;
            {var subQ6=sQuery(id+"F2.wireOp",EDGE,"5d3470c4-9be6-4ab4-af18-11b8a38611c9.12.34.0");Q62=makeQuery(id+"F2.imprint","IMPRINT",FACE,{"disambiguationData":[TD([[makeQuery(id+"F2.imprint","IMPRINT",EDGE,{"derivedFrom":subQ6}),1.0]])]});}
            var Q63;
            {var subQ1=sQuery(id+"F2.wireOp",EDGE,"5d3470c4-9be6-4ab4-af18-11b8a38611c9.12.33.0");Q63=makeQuery(id+"F2.imprint","IMPRINT",FACE,{"disambiguationData":[TD([[makeQuery(id+"F2.imprint","IMPRINT",EDGE,{"derivedFrom":subQ1}),1.0]])]});}
            var Q64;
            {var subQ1=sQuery(id+"F2.wireOp",EDGE,"5d3470c4-9be6-4ab4-af18-11b8a38611c9.12.32.0");Q64=makeQuery(id+"F2.imprint","IMPRINT",FACE,{"disambiguationData":[TD([[makeQuery(id+"F2.imprint","IMPRINT",EDGE,{"derivedFrom":subQ1}),1.0]])]});}
            var Q65;
            {var subQ1=sQuery(id+"F2.wireOp",EDGE,"5d3470c4-9be6-4ab4-af18-11b8a38611c9.12.31.0");Q65=makeQuery(id+"F2.imprint","IMPRINT",FACE,{"disambiguationData":[TD([[makeQuery(id+"F2.imprint","IMPRINT",EDGE,{"derivedFrom":subQ1}),1.0]])]});}
            var Q66;
            {var subQ1=sQuery(id+"F2.wireOp",EDGE,"5d3470c4-9be6-4ab4-af18-11b8a38611c9.12.30.0");Q66=makeQuery(id+"F2.imprint","IMPRINT",FACE,{"disambiguationData":[TD([[makeQuery(id+"F2.imprint","IMPRINT",EDGE,{"derivedFrom":subQ1}),1.0]])]});}
            extrude(context, id + "F3", {"entities" : qUnion([Q0, Q1, Q2, Q3, Q4, Q5, Q6, Q7, Q8, Q9, Q10, Q11, Q12, Q13, Q14, Q15, Q16, Q17, Q18, Q19, Q20, Q21, Q22, Q23, Q24, Q25, Q26, Q27, Q28, Q29, Q30, Q31, Q32, Q33, Q34, Q35, Q36, Q37, Q38, Q39, Q40, Q41, Q42, Q43, Q44, Q45, Q46, Q47, Q48, Q49, Q50, Q51, Q52, Q53, Q54, Q55, Q56, Q57, Q58, Q59, Q60, Q61, Q62, Q63, Q64, Q65, Q66]), "operationType" : NewBodyOperationType.REMOVE, "oppositeDirection" : true, "depth" : 4 * mm, "offsetDistance" : 25 * mm});
        }
        {
            var Q0;
            Q0=qCreatedBy(makeId("Front.planeOp"),FACE);
            var sketch = newSketch(context, id + "F4", { "sketchPlane" : qUnion([Q0])});
            skCircle(sketch, "E10", {"center": v(0, 6.25) * mm, "radius": 1 * mm});
            skSolve(sketch);
        }
        {
            var Q0;
            Q0=makeQuery(id+"F4.imprint","IMPRINT",FACE,{"disambiguationData":[TD([[makeQuery(id+"F4.imprint","IMPRINT",EDGE,{"derivedFrom":sQuery(id+"F4.wireOp",EDGE,"E10")}),1.0]])]});
            extrude(context, id + "F5", {"entities" : qUnion([Q0]), "operationType" : NewBodyOperationType.REMOVE, "depth" : 10 * mm, "offsetDistance" : 25 * mm, "symmetric" : true});
        }
    });
